# Revit family: Trap_Protectors-Zurn-Z8946-3-NT
name_source: partatom
category: Plumbing Fixtures
units: mm (PartAtom-declared; Revit-internal decimal feet)

## family parameters
Cut with Voids When Loaded = No
Host = Face
Maintain Annotation Orientation = No
OmniClass Number = 23.45.55.21
OmniClass Title = Drains (Wastes)
Part Type = Normal
Room Calculation Point = No
Round Connector Dimension = Use Radius
Shared = No

## types (1)
- Z8946-3-NT (PROTECTOR COMBINATION KIT)
    ADA Compliant = Yes
    Assembly Code = D2010
    CW Connection = No
    CWFU = 0
    Default Elevation = 48 "
    Description = PROTECTOR COMBINATION KIT: ONE TRAP PROTECTOR, TWO SUPPLY STOP
PROTECTORS AND ONE OFFSET DRAIN PROTECTOR
    HW Connection = No
    HWFU = 0
    Main Material = PVC - Zurn - White
    Manufacturer = Zurn
    Manufacturer Brand = Zurn Water, LLC
    Model = Z8946-3-NT
    Modified Date = 03/27/2026
    Offset Drain Protector Width = 8.375 "
    Offset Drain Protector Width Height = 4.625 "
    Outlet Connection Size (inch) = 1.5 "
    Product Documentation Link = https://files.zurn.com
    Product Page URL = https://www.zurn.com
    Product data URL = https://bimobject.com
    Supply Stop Height = 10 "
    Supply Stop Protector = 5.5 "
    Trap Outlet pipe Length = 8.25 "
    Trap Protector Height = 13.5 "
    URL = https://www.zurn.com
    Vent Connection = No
    WFU = 1
    Waste Connection = Yes

## geometry (parser evidence)
native form markers: Blend x4, Sweep x11
no freeform markers — native parametric forms only
